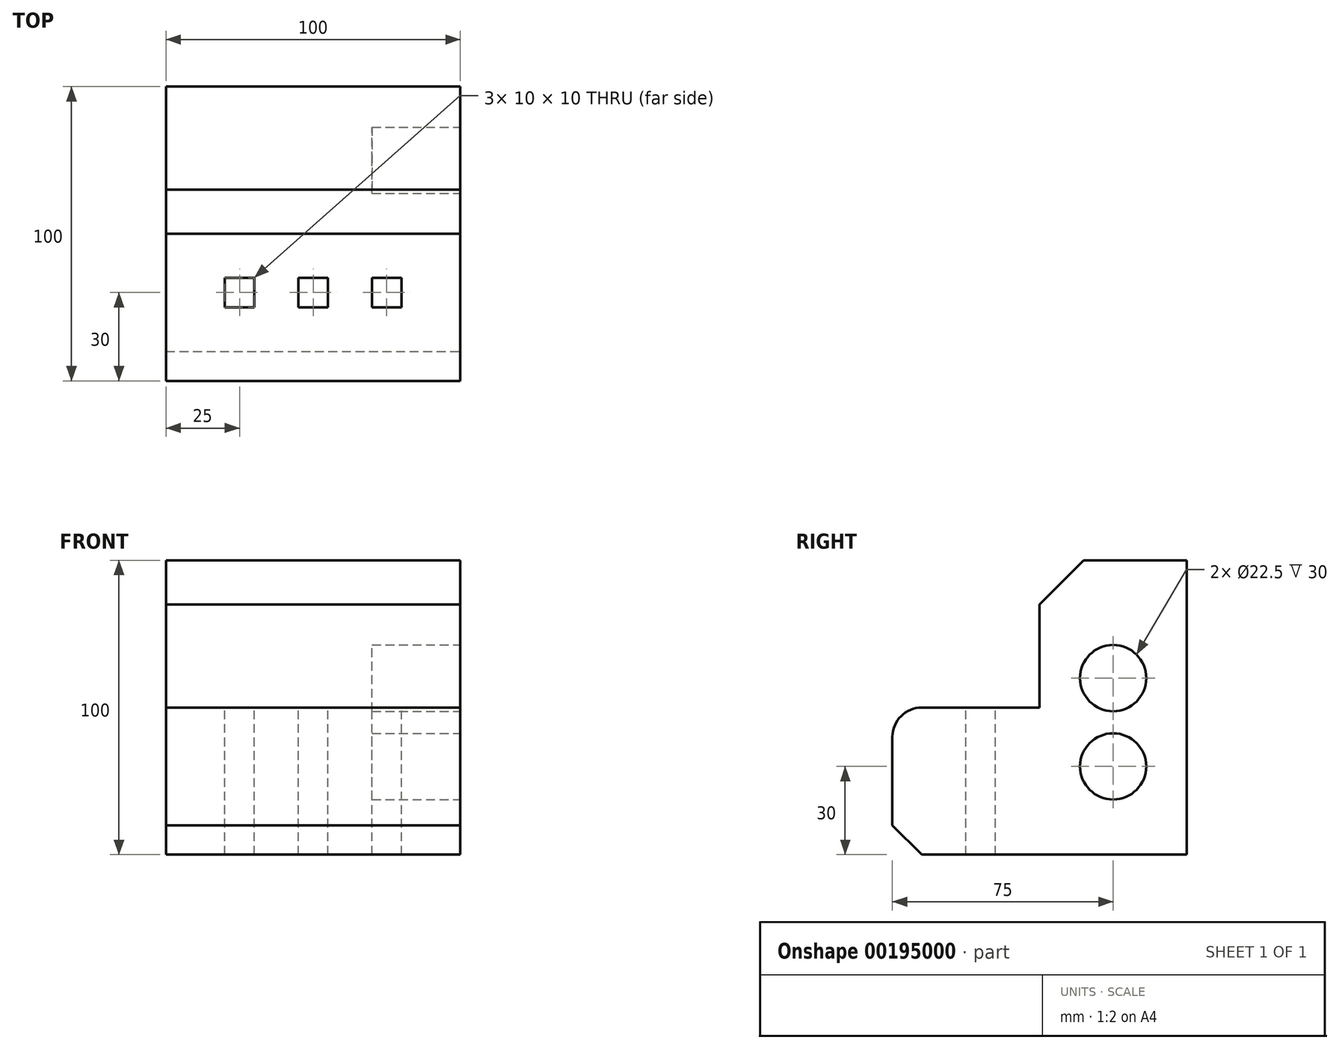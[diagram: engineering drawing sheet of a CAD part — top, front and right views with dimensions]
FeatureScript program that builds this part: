
annotation { "Feature Type Name" : "Feature", "Feature Type Description" : "" }
export const myFeature = defineFeature(function(context is Context, id is Id, definition is map)
    precondition{}
    {
        {
            var Q0;
            Q0=qCreatedBy(makeId("Top.planeOp"),FACE);
            var sketch = newSketch(context, id + "F0", { "sketchPlane" : qUnion([Q0])});
            skLineSegment(sketch, "E0.bottom", {"start": v(100, -100) * mm, "end": v(0, -100) * mm});
            skLineSegment(sketch, "E0.top", {"start": v(100, 0) * mm, "end": v(0, 0) * mm});
            skLineSegment(sketch, "E0.left", {"start": v(100, -100) * mm, "end": v(100, 0) * mm});
            skLineSegment(sketch, "E0.right", {"start": v(0, -100) * mm, "end": v(0, 0) * mm});
            skSolve(sketch);
        }
        {
            var Q0;
            Q0 = qSketchRegion(id + "F0", true);
            extrude(context, id + "F1", {"entities" : qUnion([Q0]), "depth" : 100 * mm});
        }
        {
            var Q0;
            Q0=makeQuery(id+"F1.opExtrude","SWEPT_FACE",FACE,{"disambiguationData":[OSD([sQuery(id+"F0.wireOp",EDGE,"E0.left")])]});
            var sketch = newSketch(context, id + "F2", { "sketchPlane" : qUnion([Q0])});
            skLineSegment(sketch, "E1", {"start": v(-90, 0) * mm, "end": v(-100, 10) * mm});
            skLineSegment(sketch, "E2", {"start": v(-100, 10) * mm, "end": v(-100, 40) * mm});
            skLineSegment(sketch, "E3", {"start": v(-90, 50) * mm, "end": v(-50, 50) * mm});
            skLineSegment(sketch, "E4", {"start": v(-50, 50) * mm, "end": v(-50, 85) * mm});
            skLineSegment(sketch, "E5", {"start": v(-50, 85) * mm, "end": v(-35, 100) * mm});
            skLineSegment(sketch, "E6", {"start": v(-35, 100) * mm, "end": v(-35, 130.03) * mm});
            skLineSegment(sketch, "E7", {"start": v(-35, 130.03) * mm, "end": v(-148.72, 130.03) * mm});
            skLineSegment(sketch, "E8", {"start": v(-148.72, 130.03) * mm, "end": v(-148.72, -5.63) * mm});
            skLineSegment(sketch, "E9", {"start": v(-148.72, -5.63) * mm, "end": v(-88.58, -5.63) * mm});
            skLineSegment(sketch, "E10", {"start": v(-88.58, -5.63) * mm, "end": v(-90, 0) * mm});
            skPoint(sketch, "E11.visualSharp", {"position": v(-100, 50) * mm});
            skArc(sketch, "E11.filletArc", {"start": v(-90, 50) * mm, "mid": v(-97.07, 47.07) * mm, "end": v(-100, 40) * mm});
            skSolve(sketch);
        }
        {
            var Q0;
            Q0 = qSketchRegion(id + "F2", true);
            extrude(context, id + "F3", {"entities" : qUnion([Q0]), "operationType" : NewBodyOperationType.REMOVE, "oppositeDirection" : true, "depth" : 100 * mm});
        }
        {
            var Q0;
            Q0=makeQuery(id+"F1.opExtrude","SWEPT_FACE",FACE,{"disambiguationData":[OSD([sQuery(id+"F0.wireOp",EDGE,"E0.left")])]});
            var sketch = newSketch(context, id + "F4", { "sketchPlane" : qUnion([Q0])});
            skLineSegment(sketch, "E12", {"start": v(-25, 150.43) * mm, "end": v(-25, -32.06) * mm, "construction": true});
            skCircle(sketch, "E13", {"center": v(-25, 60) * mm, "radius": 11.25 * mm});
            skCircle(sketch, "E14", {"center": v(-25, 30) * mm, "radius": 11.25 * mm});
            skSolve(sketch);
        }
        {
            var Q0;
            Q0 = qSketchRegion(id + "F4", true);
            extrude(context, id + "F5", {"entities" : qUnion([Q0]), "operationType" : NewBodyOperationType.REMOVE, "oppositeDirection" : true, "depth" : 30 * mm});
        }
        {
            var Q0;
            Q0=makeQuery(id+"F3.boolean.opBoolean","COPY",FACE,{"derivedFrom":makeQuery(id+"F3.opExtrude","SWEPT_FACE",FACE,{"disambiguationData":[OSD([sQuery(id+"F2.wireOp",EDGE,"E3")])]})});
            var sketch = newSketch(context, id + "F6", { "sketchPlane" : qUnion([Q0])});
            skLineSegment(sketch, "E15.bottom", {"start": v(20, -65) * mm, "end": v(30, -65) * mm});
            skLineSegment(sketch, "E15.top", {"start": v(20, -75) * mm, "end": v(30, -75) * mm});
            skLineSegment(sketch, "E15.left", {"start": v(20, -65) * mm, "end": v(20, -75) * mm});
            skLineSegment(sketch, "E15.right", {"start": v(30, -65) * mm, "end": v(30, -75) * mm});
            skLineSegment(sketch, "E16.1.0.0", {"start": v(45, -65) * mm, "end": v(45, -75) * mm});
            skLineSegment(sketch, "E16.1.0.1", {"start": v(45, -65) * mm, "end": v(55, -65) * mm});
            skLineSegment(sketch, "E16.1.0.2", {"start": v(55, -65) * mm, "end": v(55, -75) * mm});
            skLineSegment(sketch, "E16.1.0.3", {"start": v(45, -75) * mm, "end": v(55, -75) * mm});
            skLineSegment(sketch, "E16.2.0.0", {"start": v(70, -65) * mm, "end": v(70, -75) * mm});
            skLineSegment(sketch, "E16.2.0.1", {"start": v(70, -65) * mm, "end": v(80, -65) * mm});
            skLineSegment(sketch, "E16.2.0.2", {"start": v(80, -65) * mm, "end": v(80, -75) * mm});
            skLineSegment(sketch, "E16.2.0.3", {"start": v(70, -75) * mm, "end": v(80, -75) * mm});
            skLineSegment(sketch, "E16.direction1", {"start": v(20, -75) * mm, "end": v(45, -75) * mm, "construction": true});
            skSolve(sketch);
        }
        {
            var Q0;
            Q0 = qSketchRegion(id + "F6", true);
            extrude(context, id + "F7", {"entities" : qUnion([Q0]), "operationType" : NewBodyOperationType.REMOVE, "oppositeDirection" : true, "depth" : 50 * mm});
        }
    });
